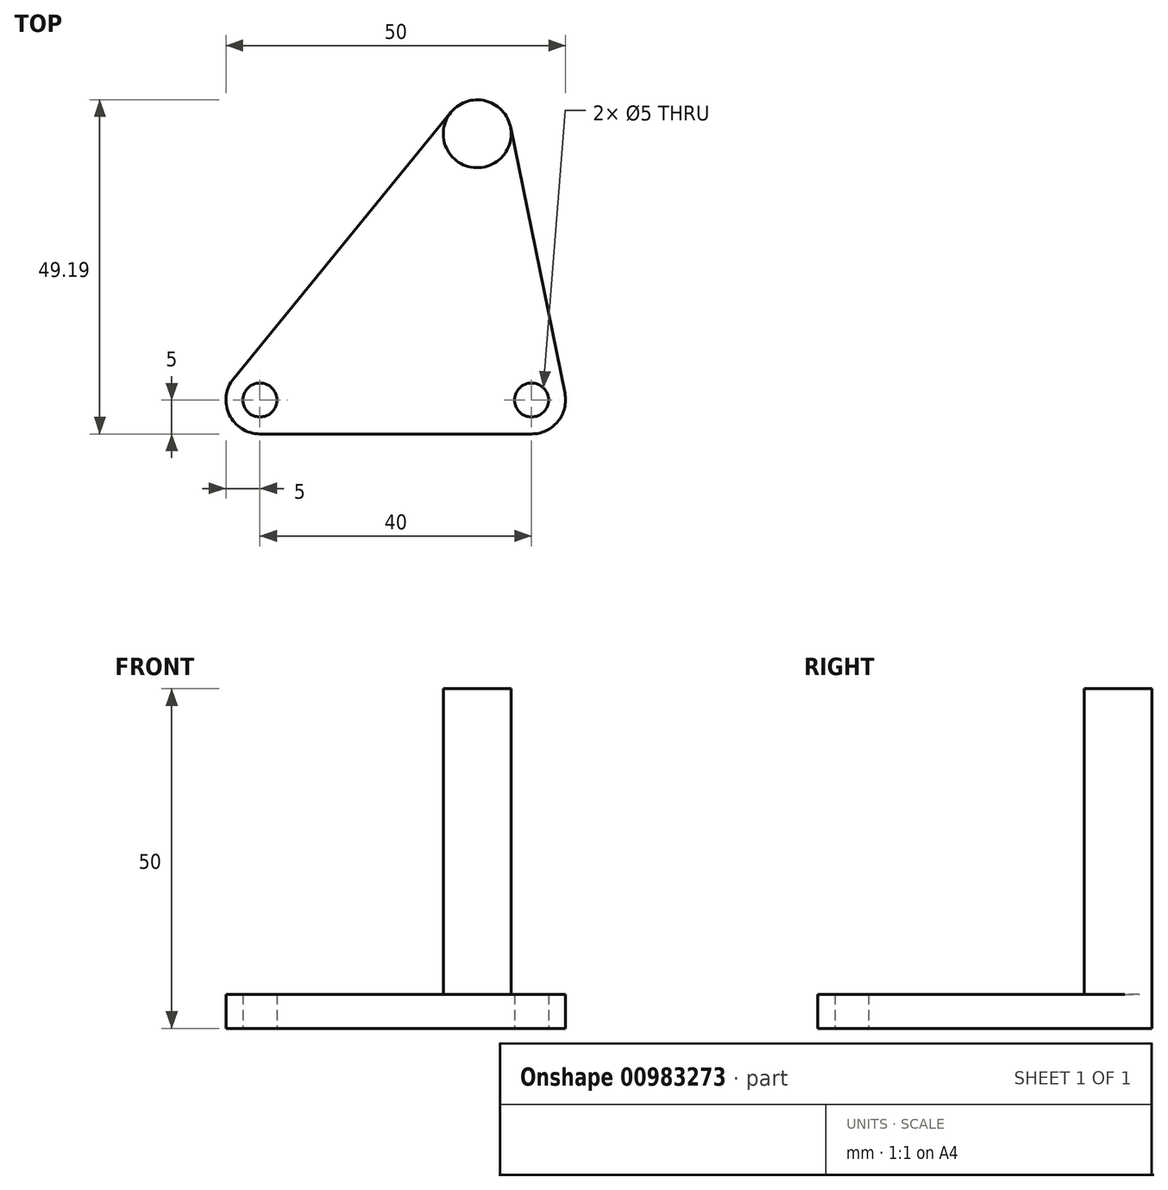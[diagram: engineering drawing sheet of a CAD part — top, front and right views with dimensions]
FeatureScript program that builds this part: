
annotation { "Feature Type Name" : "Feature", "Feature Type Description" : "" }
export const myFeature = defineFeature(function(context is Context, id is Id, definition is map)
    precondition{}
    {
        {
            var Q0;
            Q0=qCreatedBy(makeId("Top.planeOp"),FACE);
            var sketch = newSketch(context, id + "F0", { "sketchPlane" : qUnion([Q0])});
            skPoint(sketch, "E0", {"position": v(60, 0) * mm});
            skPoint(sketch, "E1", {"position": v(100, 0) * mm});
            skCircle(sketch, "E2", {"center": v(60, 0) * mm, "radius": 2.5 * mm});
            skCircle(sketch, "E3", {"center": v(100, 0) * mm, "radius": 2.5 * mm});
            skPoint(sketch, "E4", {"position": v(92, 39.2) * mm});
            skPoint(sketch, "E5", {"position": v(100, -5) * mm});
            skLineSegment(sketch, "E6", {"start": v(100, -5) * mm, "end": v(60, -5) * mm});
            skPoint(sketch, "E7", {"position": v(96.9, 40.2) * mm});
            skLineSegment(sketch, "E8", {"start": v(96.9, 40.2) * mm, "end": v(104.9, 1) * mm});
            skPoint(sketch, "E9", {"position": v(88.13, 42.35) * mm});
            skPoint(sketch, "E10", {"position": v(56.13, 3.16) * mm});
            skLineSegment(sketch, "E11", {"start": v(56.13, 3.16) * mm, "end": v(88.13, 42.35) * mm});
            skArc(sketch, "E12", {"start": v(60, -5) * mm, "mid": v(55.48, -2.14) * mm, "end": v(56.13, 3.16) * mm});
            skArc(sketch, "E13", {"start": v(88.13, 42.35) * mm, "mid": v(93.2, 44.05) * mm, "end": v(96.9, 40.2) * mm});
            skArc(sketch, "E14", {"start": v(104.9, 1) * mm, "mid": v(103.87, -3.16) * mm, "end": v(100, -5) * mm});
            skCircle(sketch, "E15", {"center": v(92, 39.2) * mm, "radius": 5 * mm});
            skSolve(sketch);
        }
        {
            var Q0;
            Q0=makeQuery(id+"F0.imprint","IMPRINT",FACE,{"disambiguationData":[TD([[makeQuery(id+"F0.imprint","IMPRINT",EDGE,{"derivedFrom":sQuery(id+"F0.wireOp",EDGE,"E2")}),-1.0]])]});
            extrude(context, id + "F1", {"entities" : qUnion([Q0]), "depth" : 5 * mm, "offsetDistance" : 25 * mm});
        }
        {
            var Q0;
            {var subQ0=sQuery(id+"F0.wireOp",EDGE,"E15");var subQ1=makeQuery(id+"F0.imprint","INTERSECT",VERTEX,{"derivedFrom":[sQuery(id+"F0.wireOp",EDGE,"E8"),subQ0]});Q0=makeQuery(id+"F0.imprint","IMPRINT",FACE,{"disambiguationData":[TD([[makeQuery(id+"F0.imprint","IMPRINT",EDGE,{"disambiguationData":[TD([[subQ1,-1.0]])],"derivedFrom":subQ0}),1.0]])]});}
            extrude(context, id + "F2", {"entities" : qUnion([Q0]), "operationType" : NewBodyOperationType.ADD, "depth" : 50 * mm, "offsetDistance" : 25 * mm});
        }
    });
